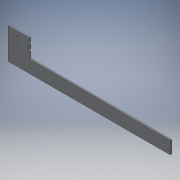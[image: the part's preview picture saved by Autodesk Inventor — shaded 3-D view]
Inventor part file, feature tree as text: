
AUTODESK INVENTOR PART (.ipt)
format: ipt  version: 2019 (Build 230136000, 136)  size: 317,440 bytes
history: native  units: in
note: dims shown in document units (in); Inventor stores cm internally (conversion verified against a paired STEP export)
features: reference x16, other x7, extrude x6, sketch x6, fillet x4, projected_geometry x1, helix x1
ambient origin geometry x8: Origin, YZ Plane, XZ Plane, XY Plane, X Axis, Y Axis, Z Axis, Center Point
bodies: Solid1 (feature_tree)
feature tree (41):
  extrude  "Extrusion1"  Depth=0.1181in
  fillet  "Fillet1"  Radius=0.1181in
  extrude  "Extrusion2"  Depth=0.1181in
  fillet  "Fillet2"  Radius=0.1181in
  fillet  "Fillet3"  Radius=0.1181in
  extrude  "Extrusion3"  Depth=0.1575in TaperAngle=0.0deg
  extrude  "Extrusion5"  Depth=0.0787in TaperAngle=0.0deg
  fillet  "Fillet5"  Radius=0.0787in
  extrude  "Extrusion6"  Depth=0.0787in
  extrude  "Extrusion7"  Depth=0.0394in
  sketch  "Sketch1"  dims[d0=0.1181in d1=0.1181in d2=0.1181in]
  reference  "Reference1"
  reference  "Reference2"
  reference  "Reference3"
  reference  "Reference4"
  reference  "Reference5"
  reference  "Reference6"
  sketch  "Sketch2"  dims[d3=0.1181in d4=0.1181in d5=0.1181in d6=0.1181in]
  projected_geometry  "Projected Loop1"
  sketch  "Sketch3"  dims[d7=0.1181in d8=0.1575in d9=0.0in]
  reference  "Reference7"
  reference  "Reference8"
  reference  "Reference9"
  reference  "Reference10"
  reference  "Reference11"
  reference  "Reference12"
  sketch  "Sketch6"  dims[d10=0.0787in d11=1.0in d12=0.0in d13=0.0787in]
  sketch  "Sketch7"  dims[d14=0.0787in d15=0.0079in]
  reference  "Reference16"
  reference  "Reference17"
  sketch  "Sketch8"  dims[d16=0.0079in d17=0.0079in d18=0.0079in d19=0.126in d20=0.126in d21=1.0in d22=0.0in d29=0.1772in d30=16.9291in d31=1.0in d32=0.0in d33=0.0394in d34=1.0in d35=0.0in d36=1.0in d37=0.0in]
  reference  "Reference18"
  reference  "Reference19"
  other  "<userpath>\Documents\CAD Files\Helix DLP\Helix DLP.iam"
  helix  "Helix DLP.iam"  [1 undecoded]
  other  "MGN12H, LINEAR GUIDE BLOCK:2"
  other  "MGN12H, LINEAR GUIDE BLOCK:1"
  other  "motor_brace_3:4"
  other  "motor_brace_3:3"
  other  "motor_brace_3:5"
  other  "motor_brace_3:6"
note: 1 required parameter value undecoded (feature->parameter linkage not recoverable at this tier; creation-order binding heuristic only, values carry confidence <= 0.55)
